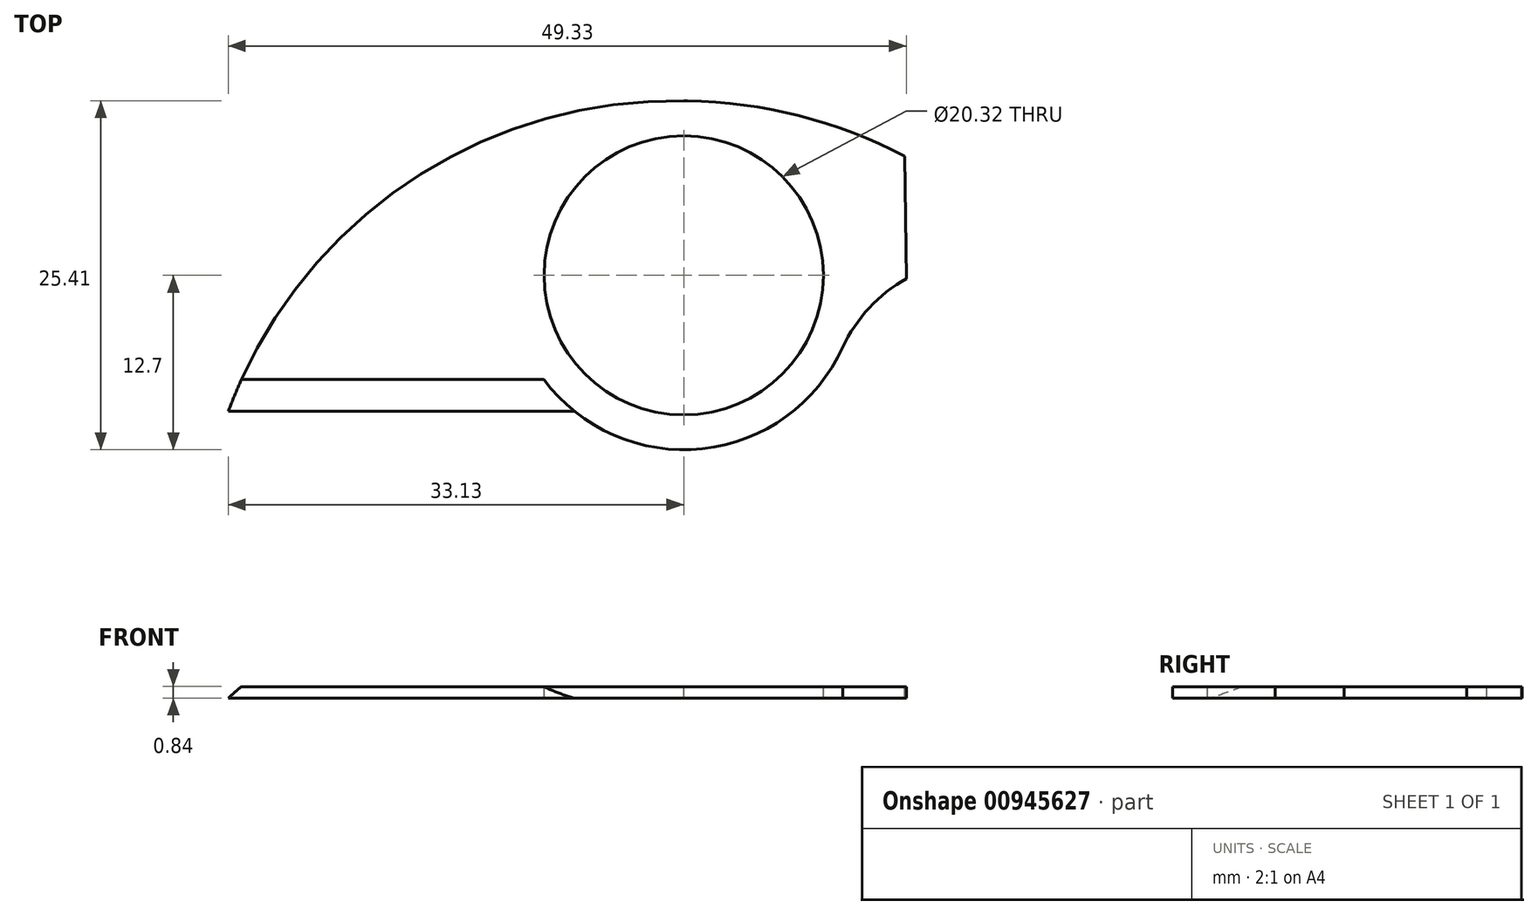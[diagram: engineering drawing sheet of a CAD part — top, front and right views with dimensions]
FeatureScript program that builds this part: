
annotation { "Feature Type Name" : "Feature", "Feature Type Description" : "" }
export const myFeature = defineFeature(function(context is Context, id is Id, definition is map)
    precondition{}
    {
        {
            var Q0;
            Q0=qCreatedBy(makeId("Top.planeOp"),FACE);
            var sketch = newSketch(context, id + "F0", { "sketchPlane" : qUnion([Q0])});
            skCircle(sketch, "E0", {"center": v(0, 0) * mm, "radius": 12.7 * mm});
            skSolve(sketch);
        }
        {
            var Q0;
            Q0=qSketchRegion(id+"F0",true);
            extrude(context, id + "F1", {"entities" : qUnion([Q0]), "depth" : 0.84 * mm, "offsetDistance" : 25.4 * mm});
        }
        {
            var Q0;
            Q0=makeQuery(id+"F1.opExtrude","CAP_FACE",FACE,{"disambiguationData":[OSD([sQuery(id+"F0.wireOp",EDGE,"E0")])],"isStart":false});
            var sketch = newSketch(context, id + "F2", { "sketchPlane" : qUnion([Q0])});
            skLineSegment(sketch, "E1", {"start": v(-7.78, -10.04) * mm, "end": v(-33.18, -10.04) * mm});
            skArc(sketch, "E2", {"start": v(0, 12.7) * mm, "mid": v(-20.23, 6.65) * mm, "end": v(-33.18, -10.04) * mm});
            skSolve(sketch);
        }
        {
            var Q0;
            {var subQ0=makeQuery(id+"F1.opExtrude","CAP_EDGE",EDGE,{"disambiguationData":[OSD([sQuery(id+"F0.wireOp",EDGE,"E0")])],"isStart":false});var subQ1=makeQuery(id+"F2.imprint","INTERSECT",VERTEX,{"derivedFrom":[subQ0,sQuery(id+"F2.wireOp",EDGE,"E1")]});Q0=makeQuery(id+"F2.imprint","IMPRINT",FACE,{"disambiguationData":[TD([[makeQuery(id+"F2.imprint","IMPRINT",EDGE,{"disambiguationData":[TD([[subQ1,-1.0]])],"derivedFrom":subQ0}),1.0]])]});}
            var sketch = newSketch(context, id + "F3", { "sketchPlane" : qUnion([Q0])});
            skCircle(sketch, "E3.0", {"center": v(0, 0) * mm, "radius": 10.16 * mm});
            skSolve(sketch);
        }
        {
            var Q0;
            Q0=makeQuery(id+"F3.imprint","IMPRINT",FACE,{"disambiguationData":[TD([[makeQuery(id+"F3.imprint","IMPRINT",EDGE,{"derivedFrom":sQuery(id+"F3.wireOp",EDGE,"E3.0")}),1.0]])]});
            extrude(context, id + "F4", {"entities" : qUnion([Q0]), "operationType" : NewBodyOperationType.REMOVE, "oppositeDirection" : true, "depth" : 18.29 * mm, "offsetDistance" : 25.4 * mm});
        }
        {
            var Q0;
            {var subQ0=sQuery(id+"F2.wireOp",EDGE,"E1");Q0=makeQuery(id+"F2.imprint","IMPRINT",FACE,{"disambiguationData":[TD([[makeQuery(id+"F2.imprint","IMPRINT",EDGE,{"derivedFrom":subQ0}),-1.0]])]});}
            extrude(context, id + "F5", {"entities" : qUnion([Q0]), "operationType" : NewBodyOperationType.ADD, "oppositeDirection" : true, "depth" : 0.84 * mm, "offsetDistance" : 25.4 * mm});
        }
        {
            var Q0;
            {var subQ0=sQuery(id+"F0.wireOp",EDGE,"E0");Q0=makeQuery(id+"F5.boolean.opBoolean","MERGE",FACE,{"derivedFrom":[makeQuery(id+"F1.opExtrude","CAP_FACE",FACE,{"disambiguationData":[OSD([subQ0])],"isStart":false}),makeQuery(id+"F5.opExtrude","CAP_FACE",FACE,{"disambiguationData":[OSD([subQ0,sQuery(id+"F2.wireOp",EDGE,"E1"),sQuery(id+"F2.wireOp",EDGE,"E2")])],"isStart":true})]});}
            var sketch = newSketch(context, id + "F6", { "sketchPlane" : qUnion([Q0])});
            skArc(sketch, "E4", {"start": v(26.78, 0) * mm, "mid": v(18, 0.58) * mm, "end": v(11.5, -5.37) * mm});
            skArc(sketch, "E5", {"start": v(26.78, 0) * mm, "mid": v(14.8, 9.32) * mm, "end": v(0, 12.7) * mm});
            skSolve(sketch);
        }
        {
            var Q0;
            {var subQ0=sQuery(id+"F6.wireOp",EDGE,"E5");var subQ1=sQuery(id+"F6.wireOp",EDGE,"E4");var subQ2=makeQuery(id+"F6.imprint","INTERSECT",VERTEX,{"derivedFrom":[subQ1,subQ0]});Q0=makeQuery(id+"F6.imprint","IMPRINT",FACE,{"disambiguationData":[TD([[makeQuery(id+"F6.imprint","IMPRINT",EDGE,{"disambiguationData":[TD([[subQ2,-1.0]])],"derivedFrom":subQ1}),-1.0]])]});}
            extrude(context, id + "F7", {"entities" : qUnion([Q0]), "operationType" : NewBodyOperationType.ADD, "oppositeDirection" : true, "depth" : 0.84 * mm, "offsetDistance" : 25.4 * mm});
        }
        {
            var Q0;
            Q0=makeQuery(id+"F7.opExtrude","SWEPT_EDGE",EDGE,{"disambiguationData":[OSD([sQuery(id+"F6.wireOp",EDGE,"E4"),sQuery(id+"F6.wireOp",EDGE,"E5")])]});
            chamfer(context, id + "F8", {"entities" : qUnion([Q0]), "width" : 5.08 * mm, "tangentPropagation" : true});
        }
        {
            var Q0;
            Q0=makeQuery(id+"F5.opExtrude","CAP_EDGE",EDGE,{"disambiguationData":[OSD([sQuery(id+"F2.wireOp",EDGE,"E1")])],"isStart":true});
            chamfer(context, id + "F9", {"entities" : qUnion([Q0]), "chamferType" : ChamferType.OFFSET_ANGLE, "width" : 0.89 * mm, "oppositeDirection" : false, "angle" : 70 * degree, "tangentPropagation" : true});
        }
    });
